# Revit family: Base_Cabinet-Danver-Blind_Corner_Base_BCBxx11
name_source: partatom
category: Casework
units: mm (PartAtom-declared; Revit-internal decimal feet)

## family parameters
Always vertical = Yes
Classification Number = 23.40.35.17.47
Cut with Voids When Loaded = No
Room Calculation Point = No
Shared = No
Work Plane-Based = No

## types (1)
- Not a Type - Load Type Catalog
    Assembly Code = E2010.30
    C_Foot = No
    Cabinet Depth = 2' - 0"
    Cabinet Height = 2' - 6"
    Cabinet Material = Metal - Danver - Stainless Steel
    Construction Type = 304 Grade Stainless Steel
    Default Elevation = 0' - 0"
    Depth = 0' - 0"
    Door Material = Metal - Danver - Stainless Steel
    Drawer Height = 0' - 6 1/8"
    Drawer Material = Metal - Danver - Stainless Steel
    Flat Drawer Material = Metal - Danver - Stainless Steel
    Handle Material = Metal - Danver - Chrome Plated Steel
    Height = 2' - 0"
    Instruction Sheet Link = https://danver.com
    Keynote = 12 31 00
    Manufacturer = Danver Outdoor Kitchens
    Model = Not a Type - Load Type Catalog
    Product Documentation Link = https://danver.com
    Product Name = Bind Corner Base
    Product Page URL = https://danver.com
    Toe Kick Material = Metal - Danver - Toe Kick
    Total Width = 2' - 6"
    URL = www.danver.com
    V_Drawer = Yes
    Version = 2020 - V0.0a
    Warranty URL = https://danver.com
    Width = 1' - 3"

## geometry (parser evidence)
native form markers: Sweep x18
no freeform markers — native parametric forms only
